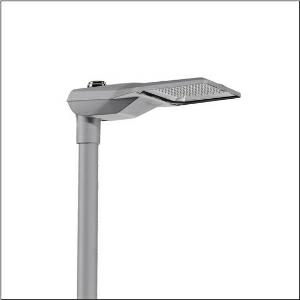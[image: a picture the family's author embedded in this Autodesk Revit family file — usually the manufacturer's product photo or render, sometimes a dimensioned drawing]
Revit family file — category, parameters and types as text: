
# Revit family: streetlight_sl_21_midi___st0_8a_5xe7c37n08lb_f1b7
name_source: partatom
category: Lighting Fixtures
units: mm (PartAtom-declared; Revit-internal decimal feet)

## family parameters
Cut with Voids When Loaded = No
Host = Face
Light Source = No
Part Type = Normal
Room Calculation Point = No
Round Connector Dimension = Use Diameter
Shared = No

## types (1)
- --- (1 x LED, 14340 lm, 98.3 W, 3000K)
    Apparent Load = 98 VA
    CIE Flux Codes = 38 75 97 100 100
    Color Rendering = 70
    Color Temperature = 3000K
    Default Elevation = 1800 mm
    Description = Streetlight SL 21 midi, mast luminaire, primary light control with lens, of PMMA, primary optical cover: cover, of toughened safety glass, transparent, light distribution: ST0.8a, light emission: direct distribution, primary light characteristic: asymmetric, installation type: side-entry, LED, 3G 2.5mm², High Power LED, rated luminous flux: 14.340lm, luminous efficacy: 146lm/W, light colour: 730, colour temperature: 3000K, control gear: NEMA (7pin), control: overheat protection, pre-setting: linear dimming characteristic, constant luminous flux control, time-dependent luminous flux control, flexible luminous flux parameterisation, mains connection: 220..240V, AC, 50/60Hz, connection cable pre-assembled, cable length: 10,5m, wiring characteristics: H05VV-F, start of lifetime: 98W, end of service life: 101W, reduction: 45W, luminaire housing, of diecast aluminium (EN AC-44300), powder-coated, SITECO metallic grey (DB 702S), corrosivity category C5 high according to DIN EN ISO 12944, multi-level sealing system, sealing non-destructively replaceable, inclination adjustable: 0°, 5°, 10°, 15°, length: 644mm, width: 335mm, height: 110mm, spigot size: 42mm (side-entry), mounting height: 4..8m, protection rating (complete): IP66, insulation class (complete): insulation class I (protective earthing), certification: CE, ENEC, ENEC+, VDE, impact resistance: IK10, permissible operating ambient temperature for outdoor applications: -40..+50°C, standard-compliant lighting for roads and squares, packaging unit: 1 piece

Light Distribution: ST0.8a
    Height = 111 mm
    Lamp = 1 x LED
    Lamp Light Flux = 14340 lm
    Lamp Power = 98.3 W
    Lamp count = 1
    Length = 644 mm
    Luminous efficacy = 146 lm/W
    Manufacturer = Siteco
    ModVariant = No
    Model = 5XE7C37N08LB
    Number of Poles = 1
    OnlyDefault = Yes
    Power Factor = 1
    Product Name = Streetlight SL 21 midi | ST0.8a
    Product group = mast luminaire | pylon top
    ProductGroupID = 6100
    Protection Class = Protection class I
    Protection Degree = IP 66
    RLX_Detail_Level = 1
    RLX_Emergency_Light_Flux = 0 lm
    RLX_Emergency_Type = 0
    RLX_Emergency_Type_DB = No
    RlxData = <blob elided: 26705 chars, md5=1b17395d>
    Socket = socket
    Standby Power = 0 W
    System Light Flux = 14340 lm
    System Power = 98 W
    Type Comments = factory setting: luminous flux: 100 % | dim-lin: 254 | 1020 mA
    Type Image = l_1294377.jpg
    URL = http://relux.com
    VarID = @adj_133603
    Voltage = 0 V
    Weight = 0.00 kg
    Width = 336 mm

## geometry (parser evidence)
native form markers: Blend x4, Sweep x12
no freeform markers — native parametric forms only
